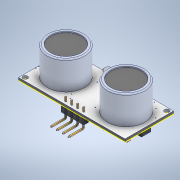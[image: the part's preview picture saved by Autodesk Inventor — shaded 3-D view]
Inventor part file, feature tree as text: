
AUTODESK INVENTOR PART (.ipt)
format: ipt  version: 2021 (Build 250183000, 183)  size: 2,011,136 bytes
history: native  units: mm
features: other x2, sketch x1
ambient origin geometry x8: Origin, YZ Plane, XZ Plane, XY Plane, X Axis, Y Axis, Z Axis, Center Point
bodies: Volumenkörper1 (feature_tree)
feature tree (3):
  other  "hc-sr04 (1).STEP"
  sketch  "Skizze1"
  parser-record x1  (decoder bookkeeping rows leaked as tree rows — omitted from the tree; the rows remain in map.json)
